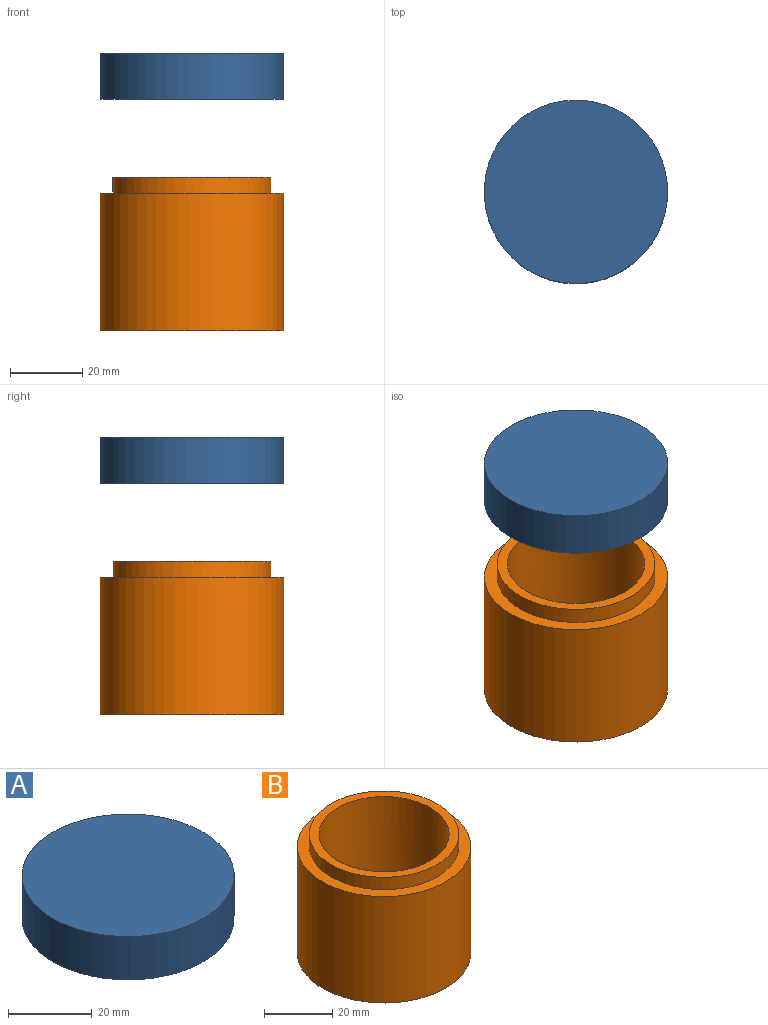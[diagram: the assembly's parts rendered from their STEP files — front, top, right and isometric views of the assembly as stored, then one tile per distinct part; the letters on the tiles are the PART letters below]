
ASSEMBLY  parts=2 mates=1
PART A: 7 faces, bbox 50.8x50.8x12.7 mm
  f0: plane 50.8x50.8mm, normal (0,0,-1), area 523.6mm2, adj f2,f4
  f1: plane 50.8x50.8mm, normal (0,0,1), area 2026.8mm2, adj f2
  f2: cylinder r=25.4mm len=50.8mm, axis (0,0,-1), area 2026.8mm2, adj f0,f1
  f3: plane 43.75x43.75mm, normal (0,0,-1), area 363.2mm2, adj f4,f6
  f4: cylinder r=21.87mm len=43.75mm, axis (0,0,1), area 607mm2, adj f0,f3
  f5: plane 38.1x38.1mm, normal (0,0,-1), area 1140.1mm2, adj f6
  f6: cylinder r=19.05mm len=38.1mm, axis (0,0,-1), area 231.4mm2, adj f3,f5
PART B: 7 faces, bbox 50.8x50.8x42.5 mm
  f0: cylinder r=25.4mm len=50.8mm, axis (0,0,-1), area 6080.5mm2, adj f1,f2
  f1: plane 50.8x50.8mm, normal (0,0,-1), area 2026.8mm2, adj f0
  f2: plane 50.8x50.8mm, normal (0,0,1), area 523.6mm2, adj f0,f4
  f3: plane 43.75x43.75mm, normal (0,0,1), area 363.2mm2, adj f4,f6
  f4: cylinder r=21.87mm len=43.75mm, axis (0,0,1), area 607mm2, adj f2,f3
  f5: plane 38.1x38.1mm, normal (0,0,1), area 1140.1mm2, adj f6
  f6: cylinder r=19.05mm len=38.1mm, axis (0,0,-1), area 4328.9mm2, adj f3,f5
PLACE A t=(0,0,25.97)mm
PLACE B at identity fixed
MATE slider A.f2 <-> B.f0  axis (0,0,1) through (0,0,64.07)mm
